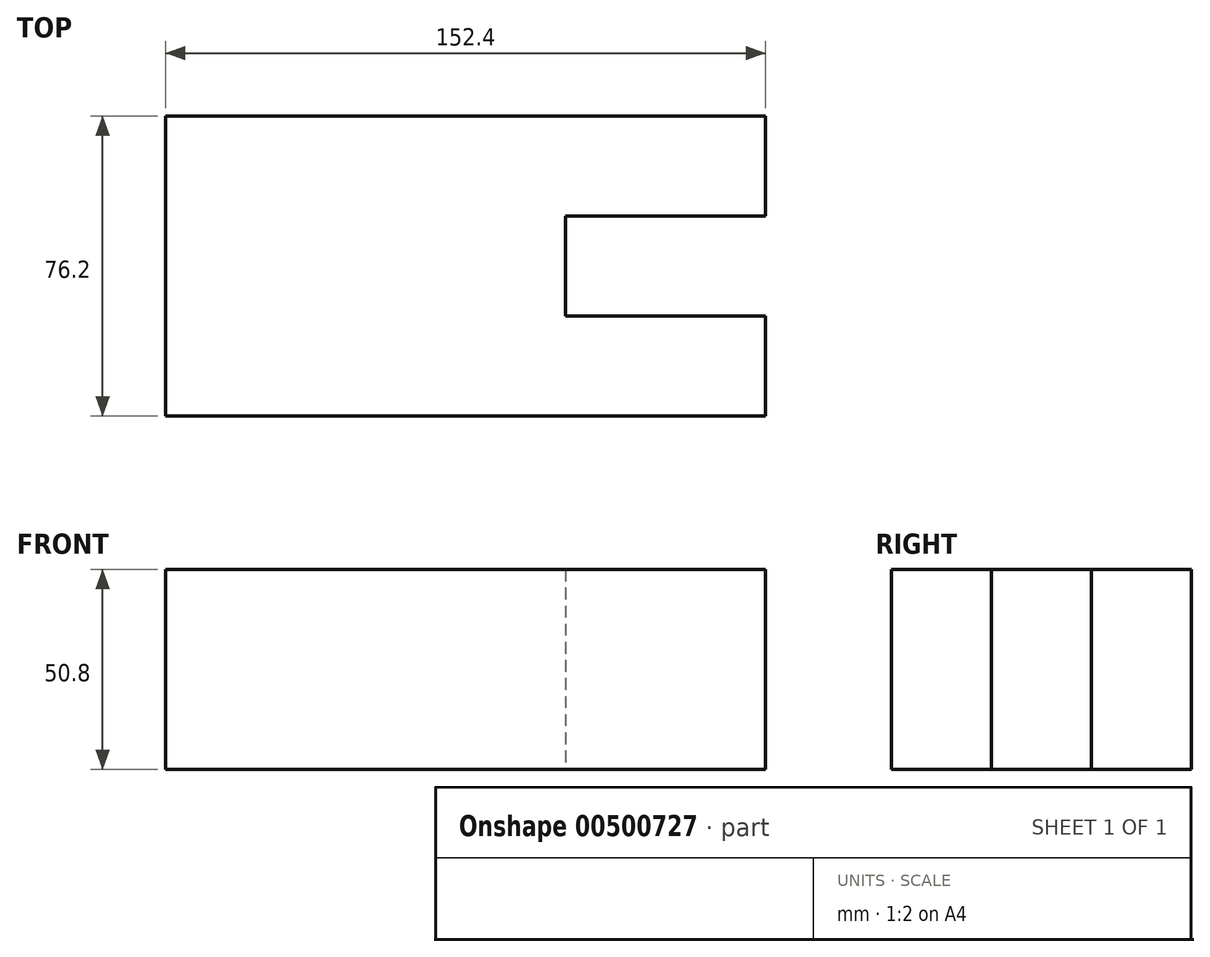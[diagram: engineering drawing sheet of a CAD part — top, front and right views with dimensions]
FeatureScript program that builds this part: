
annotation { "Feature Type Name" : "Feature", "Feature Type Description" : "" }
export const myFeature = defineFeature(function(context is Context, id is Id, definition is map)
    precondition{}
    {
        {
            var Q0;
            Q0=qCreatedBy(makeId("Top.planeOp"),FACE);
            var sketch = newSketch(context, id + "F0", { "sketchPlane" : qUnion([Q0])});
            skLineSegment(sketch, "E0.bottom", {"start": v(-85.56, 50.78) * mm, "end": v(16.04, 50.78) * mm});
            skLineSegment(sketch, "E0.top", {"start": v(-85.56, -25.42) * mm, "end": v(16.04, -25.42) * mm});
            skLineSegment(sketch, "E0.left", {"start": v(-85.56, 50.78) * mm, "end": v(-85.56, -25.42) * mm});
            skLineSegment(sketch, "E0.right", {"start": v(16.04, 50.78) * mm, "end": v(16.04, -25.42) * mm});
            skLineSegment(sketch, "E1.bottom", {"start": v(16.04, 50.78) * mm, "end": v(66.84, 50.78) * mm});
            skLineSegment(sketch, "E1.top", {"start": v(16.04, 25.38) * mm, "end": v(66.84, 25.38) * mm});
            skLineSegment(sketch, "E1.left", {"start": v(16.04, 50.78) * mm, "end": v(16.04, 25.38) * mm});
            skLineSegment(sketch, "E1.right", {"start": v(66.84, 50.78) * mm, "end": v(66.84, 25.38) * mm});
            skLineSegment(sketch, "E2.bottom", {"start": v(16.04, -0.02) * mm, "end": v(66.84, -0.02) * mm});
            skLineSegment(sketch, "E2.top", {"start": v(16.04, -25.42) * mm, "end": v(66.84, -25.42) * mm});
            skLineSegment(sketch, "E2.left", {"start": v(16.04, -0.02) * mm, "end": v(16.04, -25.42) * mm});
            skLineSegment(sketch, "E2.right", {"start": v(66.84, -0.02) * mm, "end": v(66.84, -25.42) * mm});
            skSolve(sketch);
        }
        {
            var Q0;
            Q0=makeQuery(id+"F0.imprint","IMPRINT",FACE,{"disambiguationData":[TD([[makeQuery(id+"F0.imprint","IMPRINT",EDGE,{"derivedFrom":sQuery(id+"F0.wireOp",EDGE,"E0.bottom")}),-1.0]])]});
            var Q1;
            Q1=makeQuery(id+"F0.imprint","IMPRINT",FACE,{"disambiguationData":[TD([[makeQuery(id+"F0.imprint","IMPRINT",EDGE,{"derivedFrom":sQuery(id+"F0.wireOp",EDGE,"E1.bottom")}),-1.0]])]});
            var Q2;
            Q2=makeQuery(id+"F0.imprint","IMPRINT",FACE,{"disambiguationData":[TD([[makeQuery(id+"F0.imprint","IMPRINT",EDGE,{"derivedFrom":sQuery(id+"F0.wireOp",EDGE,"E2.bottom")}),-1.0]])]});
            extrude(context, id + "F1", {"entities" : qUnion([Q0, Q1, Q2]), "depth" : 50.8 * mm});
        }
    });
